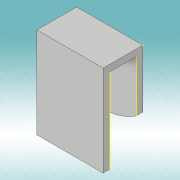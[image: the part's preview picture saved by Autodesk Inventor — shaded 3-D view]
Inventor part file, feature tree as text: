
AUTODESK INVENTOR PART (.ipt)
format: ipt  version: 2019 (Build 230136000, 136)  size: 122,880 bytes
history: native  units: mm
features: sketch x4, extrude x4
ambient origin geometry x8: Origin, YZ Plane, XZ Plane, XY Plane, X Axis, Y Axis, Z Axis, Center Point
bodies: Solid1 (feature_tree)
feature tree (8):
  sketch  "Sketch1"  dims[d14=35.0mm d15=40.0mm]
  extrude  "Extrusion1"  Depth=40.0mm
  extrude  "Extrusion2"  Depth=20.0mm
  extrude  "Extrusion3"  Depth=35.0mm
  sketch  "Sketch4"  dims[d20=4.0mm d21=0.0mm d22=4.0mm d23=40.0mm d24=16.0mm d25=0.0mm d26=55.0mm d27=40.0mm d28=4.0mm d29=0.0mm d30=0.1mm d31=0.0mm]
  extrude  "Extrusion4"  Depth=4.0mm
  sketch  "Sketch2"  dims[d16=20.0mm d17=38.0mm]
  sketch  "Sketch3"  dims[d18=18.0mm d19=35.0mm]
